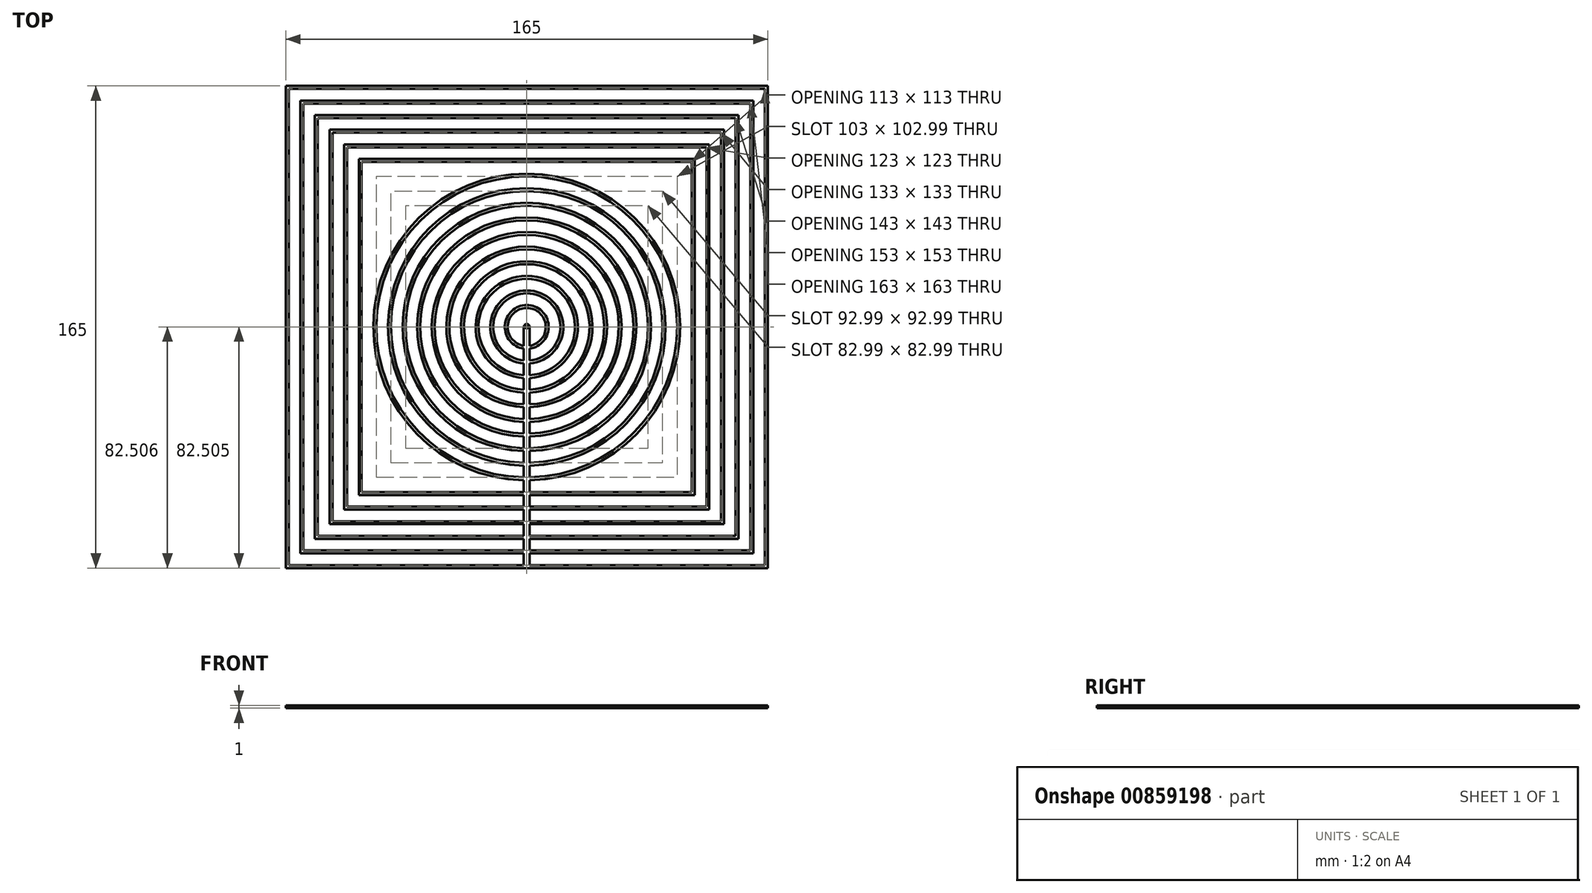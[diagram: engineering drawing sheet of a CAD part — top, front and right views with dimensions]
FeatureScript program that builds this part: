
annotation { "Feature Type Name" : "Feature", "Feature Type Description" : "" }
export const myFeature = defineFeature(function(context is Context, id is Id, definition is map)
    precondition{}
    {
        {
            var Q0;
            Q0=qCreatedBy(makeId("Top.planeOp"),FACE);
            var sketch = newSketch(context, id + "F0", { "sketchPlane" : qUnion([Q0])});
            skLineSegment(sketch, "E0.bottom", {"start": v(-81.5, -81.5) * mm, "end": v(81.5, -81.5) * mm});
            skLineSegment(sketch, "E0.top", {"start": v(-81.5, 81.5) * mm, "end": v(81.5, 81.5) * mm});
            skLineSegment(sketch, "E0.left", {"start": v(-81.5, -81.5) * mm, "end": v(-81.5, 81.5) * mm});
            skLineSegment(sketch, "E0.right", {"start": v(81.5, -81.5) * mm, "end": v(81.5, 81.5) * mm});
            skPoint(sketch, "E0.middle", {"position": v(0, 0) * mm});
            skLineSegment(sketch, "E1.bottom", {"start": v(-77.5, -77.5) * mm, "end": v(77.5, -77.5) * mm});
            skLineSegment(sketch, "E1.top", {"start": v(-77.5, 77.5) * mm, "end": v(77.5, 77.5) * mm});
            skLineSegment(sketch, "E1.left", {"start": v(-77.5, -77.5) * mm, "end": v(-77.5, 77.5) * mm});
            skLineSegment(sketch, "E1.right", {"start": v(77.5, -77.5) * mm, "end": v(77.5, 77.5) * mm});
            skLineSegment(sketch, "E2.bottom", {"start": v(-76.5, -76.5) * mm, "end": v(76.5, -76.5) * mm});
            skLineSegment(sketch, "E2.top", {"start": v(-76.5, 76.5) * mm, "end": v(76.5, 76.5) * mm});
            skLineSegment(sketch, "E2.left", {"start": v(-76.5, -76.5) * mm, "end": v(-76.5, 76.5) * mm});
            skLineSegment(sketch, "E2.right", {"start": v(76.5, -76.5) * mm, "end": v(76.5, 76.5) * mm});
            skLineSegment(sketch, "E3.bottom", {"start": v(-72.5, -72.5) * mm, "end": v(72.5, -72.5) * mm});
            skLineSegment(sketch, "E3.top", {"start": v(-72.5, 72.5) * mm, "end": v(72.5, 72.5) * mm});
            skLineSegment(sketch, "E3.left", {"start": v(-72.5, -72.5) * mm, "end": v(-72.5, 72.5) * mm});
            skLineSegment(sketch, "E3.right", {"start": v(72.5, -72.5) * mm, "end": v(72.5, 72.5) * mm});
            skLineSegment(sketch, "E4.bottom", {"start": v(-67.5, -67.5) * mm, "end": v(67.5, -67.5) * mm});
            skLineSegment(sketch, "E4.top", {"start": v(-67.5, 67.5) * mm, "end": v(67.5, 67.5) * mm});
            skLineSegment(sketch, "E4.left", {"start": v(-67.5, -67.5) * mm, "end": v(-67.5, 67.5) * mm});
            skLineSegment(sketch, "E4.right", {"start": v(67.5, -67.5) * mm, "end": v(67.5, 67.5) * mm});
            skCircle(sketch, "E5", {"center": v(0, 0) * mm, "radius": 51.5 * mm});
            skCircle(sketch, "E6", {"center": v(0, 0) * mm, "radius": 46.5 * mm});
            skCircle(sketch, "E7", {"center": v(0, 0) * mm, "radius": 41.5 * mm});
            skCircle(sketch, "E8", {"center": v(0, 0) * mm, "radius": 36.5 * mm});
            skCircle(sketch, "E9", {"center": v(0, 0) * mm, "radius": 31.5 * mm});
            skCircle(sketch, "E10", {"center": v(0, 0) * mm, "radius": 26.5 * mm});
            skLineSegment(sketch, "E11.bottom", {"start": v(-66.5, -66.5) * mm, "end": v(66.5, -66.5) * mm});
            skLineSegment(sketch, "E11.top", {"start": v(-66.5, 66.5) * mm, "end": v(66.5, 66.5) * mm});
            skLineSegment(sketch, "E11.left", {"start": v(-66.5, -66.5) * mm, "end": v(-66.5, 66.5) * mm});
            skLineSegment(sketch, "E11.right", {"start": v(66.5, -66.5) * mm, "end": v(66.5, 66.5) * mm});
            skLineSegment(sketch, "E12.bottom", {"start": v(-62.5, -62.5) * mm, "end": v(62.5, -62.5) * mm});
            skLineSegment(sketch, "E12.top", {"start": v(-62.5, 62.5) * mm, "end": v(62.5, 62.5) * mm});
            skLineSegment(sketch, "E12.left", {"start": v(-62.5, -62.5) * mm, "end": v(-62.5, 62.5) * mm});
            skLineSegment(sketch, "E12.right", {"start": v(62.5, -62.5) * mm, "end": v(62.5, 62.5) * mm});
            skLineSegment(sketch, "E13.bottom", {"start": v(-71.5, -71.5) * mm, "end": v(71.5, -71.5) * mm});
            skLineSegment(sketch, "E13.top", {"start": v(-71.5, 71.5) * mm, "end": v(71.5, 71.5) * mm});
            skLineSegment(sketch, "E13.left", {"start": v(-71.5, -71.5) * mm, "end": v(-71.5, 71.5) * mm});
            skLineSegment(sketch, "E13.right", {"start": v(71.5, -71.5) * mm, "end": v(71.5, 71.5) * mm});
            skLineSegment(sketch, "E14.bottom", {"start": v(-61.5, -61.5) * mm, "end": v(61.5, -61.5) * mm});
            skLineSegment(sketch, "E14.top", {"start": v(-61.5, 61.5) * mm, "end": v(61.5, 61.5) * mm});
            skLineSegment(sketch, "E14.left", {"start": v(-61.5, -61.5) * mm, "end": v(-61.5, 61.5) * mm});
            skLineSegment(sketch, "E14.right", {"start": v(61.5, -61.5) * mm, "end": v(61.5, 61.5) * mm});
            skLineSegment(sketch, "E15.bottom", {"start": v(-57.5, -57.5) * mm, "end": v(57.5, -57.5) * mm});
            skLineSegment(sketch, "E15.top", {"start": v(-57.5, 57.5) * mm, "end": v(57.5, 57.5) * mm});
            skLineSegment(sketch, "E15.left", {"start": v(-57.5, -57.5) * mm, "end": v(-57.5, 57.5) * mm});
            skLineSegment(sketch, "E15.right", {"start": v(57.5, -57.5) * mm, "end": v(57.5, 57.5) * mm});
            skLineSegment(sketch, "E16.bottom", {"start": v(-56.5, -56.5) * mm, "end": v(56.5, -56.5) * mm});
            skLineSegment(sketch, "E16.top", {"start": v(-56.5, 56.5) * mm, "end": v(56.5, 56.5) * mm});
            skLineSegment(sketch, "E16.left", {"start": v(-56.5, -56.5) * mm, "end": v(-56.5, 56.5) * mm});
            skLineSegment(sketch, "E16.right", {"start": v(56.5, -56.5) * mm, "end": v(56.5, 56.5) * mm});
            skCircle(sketch, "E17", {"center": v(0, 0) * mm, "radius": 21.5 * mm});
            skCircle(sketch, "E18", {"center": v(0, 0) * mm, "radius": 17.5 * mm});
            skCircle(sketch, "E19", {"center": v(0, 0) * mm, "radius": 16.5 * mm});
            skCircle(sketch, "E20", {"center": v(0, 0) * mm, "radius": 22.5 * mm});
            skCircle(sketch, "E21", {"center": v(0, 0) * mm, "radius": 27.5 * mm});
            skCircle(sketch, "E22", {"center": v(0, 0) * mm, "radius": 32.5 * mm});
            skCircle(sketch, "E23", {"center": v(0, 0) * mm, "radius": 37.5 * mm});
            skCircle(sketch, "E24", {"center": v(0, 0) * mm, "radius": 42.5 * mm});
            skCircle(sketch, "E25", {"center": v(0, 0) * mm, "radius": 47.5 * mm});
            skCircle(sketch, "E26", {"center": v(0, 0) * mm, "radius": 52.5 * mm});
            skLineSegment(sketch, "E27.bottom", {"start": v(-82.5, -82.5) * mm, "end": v(82.5, -82.5) * mm});
            skLineSegment(sketch, "E27.top", {"start": v(-82.5, 82.5) * mm, "end": v(82.5, 82.5) * mm});
            skLineSegment(sketch, "E27.left", {"start": v(-82.5, -82.5) * mm, "end": v(-82.5, 82.5) * mm});
            skLineSegment(sketch, "E27.right", {"start": v(82.5, -82.5) * mm, "end": v(82.5, 82.5) * mm});
            skCircle(sketch, "E28", {"center": v(0, 0) * mm, "radius": 12.5 * mm});
            skCircle(sketch, "E29", {"center": v(0, 0) * mm, "radius": 11.5 * mm});
            skCircle(sketch, "E30", {"center": v(0, 0) * mm, "radius": 7.5 * mm});
            skCircle(sketch, "E31", {"center": v(0, 0) * mm, "radius": 6.5 * mm});
            skCircle(sketch, "E32", {"center": v(0, 0) * mm, "radius": 1 * mm});
            skCircle(sketch, "E33", {"center": v(0, 0) * mm, "radius": 0.5 * mm});
            skLineSegment(sketch, "E34", {"start": v(1, 0) * mm, "end": v(1, -52.5) * mm});
            skLineSegment(sketch, "E35", {"start": v(-1, 0) * mm, "end": v(-1, -52.5) * mm});
            skLineSegment(sketch, "E36", {"start": v(1, -52.5) * mm, "end": v(1, -82.5) * mm});
            skLineSegment(sketch, "E37", {"start": v(-1, -52.5) * mm, "end": v(-1, -82.5) * mm});
            skSolve(sketch);
        }
        {
            var Q0;
            Q0=makeQuery(id+"F0.imprint","IMPRINT",FACE,{"disambiguationData":[TD([[makeQuery(id+"F0.imprint","IMPRINT",EDGE,{"derivedFrom":sQuery(id+"F0.wireOp",EDGE,"E5")}),-1.0]])]});
            var Q1;
            Q1=makeQuery(id+"F0.imprint","IMPRINT",FACE,{"disambiguationData":[TD([[makeQuery(id+"F0.imprint","IMPRINT",EDGE,{"derivedFrom":sQuery(id+"F0.wireOp",EDGE,"E6")}),-1.0]])]});
            var Q2;
            Q2=makeQuery(id+"F0.imprint","IMPRINT",FACE,{"disambiguationData":[TD([[makeQuery(id+"F0.imprint","IMPRINT",EDGE,{"derivedFrom":sQuery(id+"F0.wireOp",EDGE,"E7")}),-1.0]])]});
            var Q3;
            Q3=makeQuery(id+"F0.imprint","IMPRINT",FACE,{"disambiguationData":[TD([[makeQuery(id+"F0.imprint","IMPRINT",EDGE,{"derivedFrom":sQuery(id+"F0.wireOp",EDGE,"E8")}),-1.0]])]});
            var Q4;
            Q4=makeQuery(id+"F0.imprint","IMPRINT",FACE,{"disambiguationData":[TD([[makeQuery(id+"F0.imprint","IMPRINT",EDGE,{"derivedFrom":sQuery(id+"F0.wireOp",EDGE,"E9")}),-1.0]])]});
            var Q5;
            Q5=makeQuery(id+"F0.imprint","IMPRINT",FACE,{"disambiguationData":[TD([[makeQuery(id+"F0.imprint","IMPRINT",EDGE,{"derivedFrom":sQuery(id+"F0.wireOp",EDGE,"E10")}),-1.0]])]});
            var Q6;
            Q6=makeQuery(id+"F0.imprint","IMPRINT",FACE,{"disambiguationData":[TD([[makeQuery(id+"F0.imprint","IMPRINT",EDGE,{"derivedFrom":sQuery(id+"F0.wireOp",EDGE,"E17")}),-1.0]])]});
            var Q7;
            Q7=makeQuery(id+"F0.imprint","IMPRINT",FACE,{"disambiguationData":[TD([[makeQuery(id+"F0.imprint","IMPRINT",EDGE,{"derivedFrom":sQuery(id+"F0.wireOp",EDGE,"E18")}),1.0]])]});
            var Q8;
            Q8=makeQuery(id+"F0.imprint","IMPRINT",FACE,{"disambiguationData":[TD([[makeQuery(id+"F0.imprint","IMPRINT",EDGE,{"derivedFrom":sQuery(id+"F0.wireOp",EDGE,"E28")}),1.0]])]});
            var Q9;
            Q9=makeQuery(id+"F0.imprint","IMPRINT",FACE,{"disambiguationData":[TD([[makeQuery(id+"F0.imprint","IMPRINT",EDGE,{"derivedFrom":sQuery(id+"F0.wireOp",EDGE,"E30")}),1.0]])]});
            var Q10;
            Q10=makeQuery(id+"F0.imprint","IMPRINT",FACE,{"disambiguationData":[TD([[makeQuery(id+"F0.imprint","IMPRINT",EDGE,{"derivedFrom":sQuery(id+"F0.wireOp",EDGE,"E32")}),1.0]])]});
            var Q11;
            {var subQ0=sQuery(id+"F0.wireOp",EDGE,"E34");var subQ1=sQuery(id+"F0.wireOp",EDGE,"E31");var subQ2=makeQuery(id+"F0.imprint","INTERSECT",VERTEX,{"derivedFrom":[subQ1,subQ0]});Q11=makeQuery(id+"F0.imprint","IMPRINT",FACE,{"disambiguationData":[TD([[makeQuery(id+"F0.imprint","IMPRINT",EDGE,{"disambiguationData":[TD([[subQ2,1.0]])],"derivedFrom":subQ1}),1.0]])]});}
            var Q12;
            {var subQ0=sQuery(id+"F0.wireOp",EDGE,"E34");var subQ1=sQuery(id+"F0.wireOp",EDGE,"E29");var subQ2=makeQuery(id+"F0.imprint","INTERSECT",VERTEX,{"derivedFrom":[subQ1,subQ0]});Q12=makeQuery(id+"F0.imprint","IMPRINT",FACE,{"disambiguationData":[TD([[makeQuery(id+"F0.imprint","IMPRINT",EDGE,{"disambiguationData":[TD([[subQ2,1.0]])],"derivedFrom":subQ1}),1.0]])]});}
            var Q13;
            {var subQ0=sQuery(id+"F0.wireOp",EDGE,"E34");var subQ1=sQuery(id+"F0.wireOp",EDGE,"E19");var subQ2=makeQuery(id+"F0.imprint","INTERSECT",VERTEX,{"derivedFrom":[subQ1,subQ0]});Q13=makeQuery(id+"F0.imprint","IMPRINT",FACE,{"disambiguationData":[TD([[makeQuery(id+"F0.imprint","IMPRINT",EDGE,{"disambiguationData":[TD([[subQ2,1.0]])],"derivedFrom":subQ1}),1.0]])]});}
            var Q14;
            {var subQ0=sQuery(id+"F0.wireOp",EDGE,"E34");var subQ1=sQuery(id+"F0.wireOp",EDGE,"E17");var subQ2=makeQuery(id+"F0.imprint","INTERSECT",VERTEX,{"derivedFrom":[subQ1,subQ0]});Q14=makeQuery(id+"F0.imprint","IMPRINT",FACE,{"disambiguationData":[TD([[makeQuery(id+"F0.imprint","IMPRINT",EDGE,{"disambiguationData":[TD([[subQ2,1.0]])],"derivedFrom":subQ1}),1.0]])]});}
            var Q15;
            {var subQ0=sQuery(id+"F0.wireOp",EDGE,"E34");var subQ1=sQuery(id+"F0.wireOp",EDGE,"E10");var subQ2=makeQuery(id+"F0.imprint","INTERSECT",VERTEX,{"derivedFrom":[subQ1,subQ0]});Q15=makeQuery(id+"F0.imprint","IMPRINT",FACE,{"disambiguationData":[TD([[makeQuery(id+"F0.imprint","IMPRINT",EDGE,{"disambiguationData":[TD([[subQ2,1.0]])],"derivedFrom":subQ1}),1.0]])]});}
            var Q16;
            {var subQ0=sQuery(id+"F0.wireOp",EDGE,"E34");var subQ1=sQuery(id+"F0.wireOp",EDGE,"E9");var subQ2=makeQuery(id+"F0.imprint","INTERSECT",VERTEX,{"derivedFrom":[subQ1,subQ0]});Q16=makeQuery(id+"F0.imprint","IMPRINT",FACE,{"disambiguationData":[TD([[makeQuery(id+"F0.imprint","IMPRINT",EDGE,{"disambiguationData":[TD([[subQ2,1.0]])],"derivedFrom":subQ1}),1.0]])]});}
            var Q17;
            {var subQ0=sQuery(id+"F0.wireOp",EDGE,"E34");var subQ1=sQuery(id+"F0.wireOp",EDGE,"E8");var subQ2=makeQuery(id+"F0.imprint","INTERSECT",VERTEX,{"derivedFrom":[subQ1,subQ0]});Q17=makeQuery(id+"F0.imprint","IMPRINT",FACE,{"disambiguationData":[TD([[makeQuery(id+"F0.imprint","IMPRINT",EDGE,{"disambiguationData":[TD([[subQ2,1.0]])],"derivedFrom":subQ1}),1.0]])]});}
            var Q18;
            {var subQ0=sQuery(id+"F0.wireOp",EDGE,"E34");var subQ1=sQuery(id+"F0.wireOp",EDGE,"E7");var subQ2=makeQuery(id+"F0.imprint","INTERSECT",VERTEX,{"derivedFrom":[subQ1,subQ0]});Q18=makeQuery(id+"F0.imprint","IMPRINT",FACE,{"disambiguationData":[TD([[makeQuery(id+"F0.imprint","IMPRINT",EDGE,{"disambiguationData":[TD([[subQ2,1.0]])],"derivedFrom":subQ1}),1.0]])]});}
            var Q19;
            {var subQ0=sQuery(id+"F0.wireOp",EDGE,"E34");var subQ1=sQuery(id+"F0.wireOp",EDGE,"E6");var subQ2=makeQuery(id+"F0.imprint","INTERSECT",VERTEX,{"derivedFrom":[subQ1,subQ0]});Q19=makeQuery(id+"F0.imprint","IMPRINT",FACE,{"disambiguationData":[TD([[makeQuery(id+"F0.imprint","IMPRINT",EDGE,{"disambiguationData":[TD([[subQ2,1.0]])],"derivedFrom":subQ1}),1.0]])]});}
            var Q20;
            {var subQ0=sQuery(id+"F0.wireOp",EDGE,"E34");var subQ1=sQuery(id+"F0.wireOp",EDGE,"E5");var subQ2=makeQuery(id+"F0.imprint","INTERSECT",VERTEX,{"derivedFrom":[subQ1,subQ0]});Q20=makeQuery(id+"F0.imprint","IMPRINT",FACE,{"disambiguationData":[TD([[makeQuery(id+"F0.imprint","IMPRINT",EDGE,{"disambiguationData":[TD([[subQ2,1.0]])],"derivedFrom":subQ1}),1.0]])]});}
            var Q21;
            {var subQ0=sQuery(id+"F0.wireOp",EDGE,"E37");var subQ1=sQuery(id+"F0.wireOp",EDGE,"E16.bottom");var subQ2=makeQuery(id+"F0.imprint","INTERSECT",VERTEX,{"derivedFrom":[subQ1,subQ0]});Q21=makeQuery(id+"F0.imprint","IMPRINT",FACE,{"disambiguationData":[TD([[makeQuery(id+"F0.imprint","IMPRINT",EDGE,{"disambiguationData":[TD([[subQ2,-1.0]])],"derivedFrom":subQ1}),1.0]])]});}
            var Q22;
            {var subQ0=sQuery(id+"F0.wireOp",EDGE,"E37");var subQ1=sQuery(id+"F0.wireOp",EDGE,"E15.bottom");var subQ2=makeQuery(id+"F0.imprint","INTERSECT",VERTEX,{"derivedFrom":[subQ1,subQ0]});Q22=makeQuery(id+"F0.imprint","IMPRINT",FACE,{"disambiguationData":[TD([[makeQuery(id+"F0.imprint","IMPRINT",EDGE,{"disambiguationData":[TD([[subQ2,-1.0]])],"derivedFrom":subQ1}),1.0]])]});}
            var Q23;
            {var subQ0=sQuery(id+"F0.wireOp",EDGE,"E37");var subQ1=sQuery(id+"F0.wireOp",EDGE,"E14.bottom");var subQ2=makeQuery(id+"F0.imprint","INTERSECT",VERTEX,{"derivedFrom":[subQ1,subQ0]});Q23=makeQuery(id+"F0.imprint","IMPRINT",FACE,{"disambiguationData":[TD([[makeQuery(id+"F0.imprint","IMPRINT",EDGE,{"disambiguationData":[TD([[subQ2,-1.0]])],"derivedFrom":subQ1}),1.0]])]});}
            var Q24;
            {var subQ0=sQuery(id+"F0.wireOp",EDGE,"E37");var subQ1=sQuery(id+"F0.wireOp",EDGE,"E12.bottom");var subQ2=makeQuery(id+"F0.imprint","INTERSECT",VERTEX,{"derivedFrom":[subQ1,subQ0]});Q24=makeQuery(id+"F0.imprint","IMPRINT",FACE,{"disambiguationData":[TD([[makeQuery(id+"F0.imprint","IMPRINT",EDGE,{"disambiguationData":[TD([[subQ2,-1.0]])],"derivedFrom":subQ1}),1.0]])]});}
            var Q25;
            {var subQ0=sQuery(id+"F0.wireOp",EDGE,"E37");var subQ1=sQuery(id+"F0.wireOp",EDGE,"E11.bottom");var subQ2=makeQuery(id+"F0.imprint","INTERSECT",VERTEX,{"derivedFrom":[subQ1,subQ0]});Q25=makeQuery(id+"F0.imprint","IMPRINT",FACE,{"disambiguationData":[TD([[makeQuery(id+"F0.imprint","IMPRINT",EDGE,{"disambiguationData":[TD([[subQ2,-1.0]])],"derivedFrom":subQ1}),1.0]])]});}
            var Q26;
            {var subQ0=sQuery(id+"F0.wireOp",EDGE,"E37");var subQ1=sQuery(id+"F0.wireOp",EDGE,"E4.bottom");var subQ2=makeQuery(id+"F0.imprint","INTERSECT",VERTEX,{"derivedFrom":[subQ1,subQ0]});Q26=makeQuery(id+"F0.imprint","IMPRINT",FACE,{"disambiguationData":[TD([[makeQuery(id+"F0.imprint","IMPRINT",EDGE,{"disambiguationData":[TD([[subQ2,-1.0]])],"derivedFrom":subQ1}),1.0]])]});}
            var Q27;
            {var subQ0=sQuery(id+"F0.wireOp",EDGE,"E37");var subQ1=sQuery(id+"F0.wireOp",EDGE,"E4.bottom");var subQ2=makeQuery(id+"F0.imprint","INTERSECT",VERTEX,{"derivedFrom":[subQ1,subQ0]});Q27=makeQuery(id+"F0.imprint","IMPRINT",FACE,{"disambiguationData":[TD([[makeQuery(id+"F0.imprint","IMPRINT",EDGE,{"disambiguationData":[TD([[subQ2,-1.0]])],"derivedFrom":subQ1}),-1.0]])]});}
            var Q28;
            {var subQ0=sQuery(id+"F0.wireOp",EDGE,"E37");var subQ1=sQuery(id+"F0.wireOp",EDGE,"E3.bottom");var subQ2=makeQuery(id+"F0.imprint","INTERSECT",VERTEX,{"derivedFrom":[subQ1,subQ0]});Q28=makeQuery(id+"F0.imprint","IMPRINT",FACE,{"disambiguationData":[TD([[makeQuery(id+"F0.imprint","IMPRINT",EDGE,{"disambiguationData":[TD([[subQ2,-1.0]])],"derivedFrom":subQ1}),1.0]])]});}
            var Q29;
            {var subQ0=sQuery(id+"F0.wireOp",EDGE,"E37");var subQ1=sQuery(id+"F0.wireOp",EDGE,"E2.bottom");var subQ2=makeQuery(id+"F0.imprint","INTERSECT",VERTEX,{"derivedFrom":[subQ1,subQ0]});Q29=makeQuery(id+"F0.imprint","IMPRINT",FACE,{"disambiguationData":[TD([[makeQuery(id+"F0.imprint","IMPRINT",EDGE,{"disambiguationData":[TD([[subQ2,-1.0]])],"derivedFrom":subQ1}),1.0]])]});}
            var Q30;
            {var subQ0=sQuery(id+"F0.wireOp",EDGE,"E37");var subQ1=sQuery(id+"F0.wireOp",EDGE,"E1.bottom");var subQ2=makeQuery(id+"F0.imprint","INTERSECT",VERTEX,{"derivedFrom":[subQ1,subQ0]});Q30=makeQuery(id+"F0.imprint","IMPRINT",FACE,{"disambiguationData":[TD([[makeQuery(id+"F0.imprint","IMPRINT",EDGE,{"disambiguationData":[TD([[subQ2,-1.0]])],"derivedFrom":subQ1}),1.0]])]});}
            var Q31;
            {var subQ0=sQuery(id+"F0.wireOp",EDGE,"E37");var subQ1=sQuery(id+"F0.wireOp",EDGE,"E0.bottom");var subQ2=makeQuery(id+"F0.imprint","INTERSECT",VERTEX,{"derivedFrom":[subQ1,subQ0]});Q31=makeQuery(id+"F0.imprint","IMPRINT",FACE,{"disambiguationData":[TD([[makeQuery(id+"F0.imprint","IMPRINT",EDGE,{"disambiguationData":[TD([[subQ2,-1.0]])],"derivedFrom":subQ1}),1.0]])]});}
            var Q32;
            {var subQ0=sQuery(id+"F0.wireOp",EDGE,"E37");var subQ1=sQuery(id+"F0.wireOp",EDGE,"E0.bottom");var subQ2=makeQuery(id+"F0.imprint","INTERSECT",VERTEX,{"derivedFrom":[subQ1,subQ0]});Q32=makeQuery(id+"F0.imprint","IMPRINT",FACE,{"disambiguationData":[TD([[makeQuery(id+"F0.imprint","IMPRINT",EDGE,{"disambiguationData":[TD([[subQ2,-1.0]])],"derivedFrom":subQ1}),-1.0]])]});}
            var Q33;
            Q33=makeQuery(id+"F0.imprint","IMPRINT",FACE,{"disambiguationData":[TD([[makeQuery(id+"F0.imprint","IMPRINT",EDGE,{"derivedFrom":sQuery(id+"F0.wireOp",EDGE,"E0.top")}),1.0]])]});
            var Q34;
            Q34=makeQuery(id+"F0.imprint","IMPRINT",FACE,{"disambiguationData":[TD([[makeQuery(id+"F0.imprint","IMPRINT",EDGE,{"derivedFrom":sQuery(id+"F0.wireOp",EDGE,"E1.top")}),-1.0]])]});
            var Q35;
            Q35=makeQuery(id+"F0.imprint","IMPRINT",FACE,{"disambiguationData":[TD([[makeQuery(id+"F0.imprint","IMPRINT",EDGE,{"derivedFrom":sQuery(id+"F0.wireOp",EDGE,"E3.top")}),-1.0]])]});
            var Q36;
            Q36=makeQuery(id+"F0.imprint","IMPRINT",FACE,{"disambiguationData":[TD([[makeQuery(id+"F0.imprint","IMPRINT",EDGE,{"derivedFrom":sQuery(id+"F0.wireOp",EDGE,"E4.top")}),-1.0]])]});
            var Q37;
            Q37=makeQuery(id+"F0.imprint","IMPRINT",FACE,{"disambiguationData":[TD([[makeQuery(id+"F0.imprint","IMPRINT",EDGE,{"derivedFrom":sQuery(id+"F0.wireOp",EDGE,"E12.top")}),-1.0]])]});
            var Q38;
            Q38=makeQuery(id+"F0.imprint","IMPRINT",FACE,{"disambiguationData":[TD([[makeQuery(id+"F0.imprint","IMPRINT",EDGE,{"derivedFrom":sQuery(id+"F0.wireOp",EDGE,"E15.top")}),-1.0]])]});
            extrude(context, id + "F1", {"entities" : qUnion([Q0, Q1, Q2, Q3, Q4, Q5, Q6, Q7, Q8, Q9, Q10, Q11, Q12, Q13, Q14, Q15, Q16, Q17, Q18, Q19, Q20, Q21, Q22, Q23, Q24, Q25, Q26, Q27, Q28, Q29, Q30, Q31, Q32, Q33, Q34, Q35, Q36, Q37, Q38]), "depth" : 1 * mm, "offsetDistance" : 25 * mm});
        }
    });
